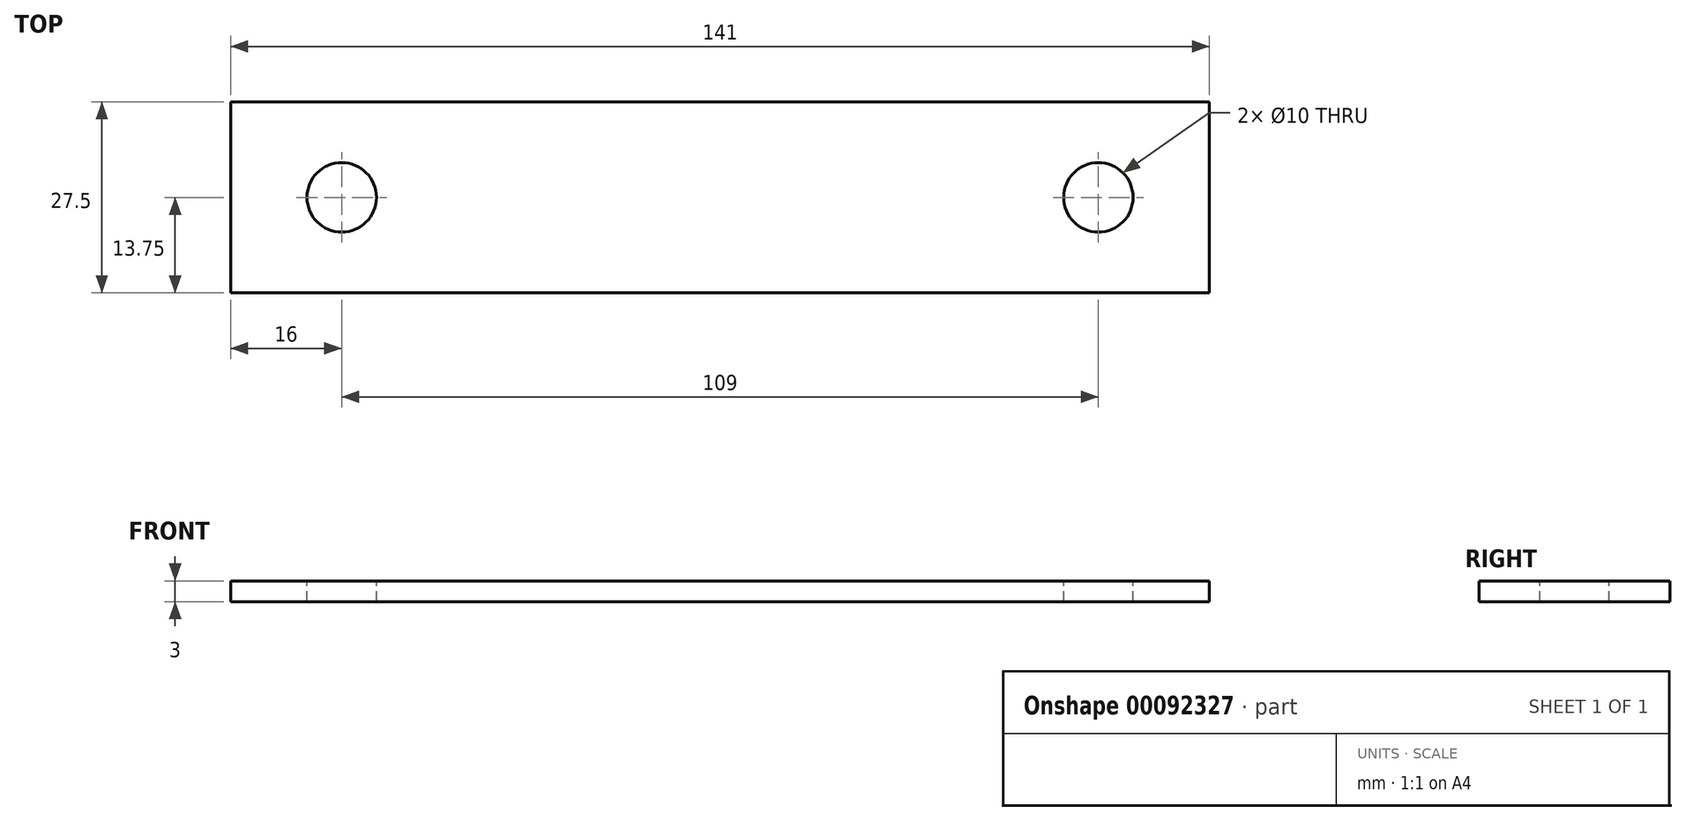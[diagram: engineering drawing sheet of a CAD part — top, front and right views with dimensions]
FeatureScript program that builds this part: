
annotation { "Feature Type Name" : "Feature", "Feature Type Description" : "" }
export const myFeature = defineFeature(function(context is Context, id is Id, definition is map)
    precondition{}
    {
        {
            var Q0;
            Q0=qCreatedBy(makeId("Top.planeOp"),FACE);
            var sketch = newSketch(context, id + "F0", { "sketchPlane" : qUnion([Q0])});
            skLineSegment(sketch, "E0.bottom", {"start": v(-70.5, 13.75) * mm, "end": v(70.5, 13.75) * mm});
            skLineSegment(sketch, "E0.top", {"start": v(-70.5, -13.75) * mm, "end": v(70.5, -13.75) * mm});
            skLineSegment(sketch, "E0.left", {"start": v(-70.5, 13.75) * mm, "end": v(-70.5, -13.75) * mm});
            skLineSegment(sketch, "E0.right", {"start": v(70.5, 13.75) * mm, "end": v(70.5, -13.75) * mm});
            skSolve(sketch);
        }
        {
            var Q0;
            Q0=makeQuery(id+"F0.imprint","IMPRINT",FACE,{"disambiguationData":[TD([[makeQuery(id+"F0.imprint","IMPRINT",EDGE,{"derivedFrom":sQuery(id+"F0.wireOp",EDGE,"E0.bottom")}),-1.0]])]});
            extrude(context, id + "F1", {"entities" : qUnion([Q0]), "endBound" : BoundingType.SYMMETRIC, "depth" : 3 * mm});
        }
        {
            var Q0;
            Q0=makeQuery(id+"F1.opExtrude","CAP_FACE",FACE,{"disambiguationData":[OSD([sQuery(id+"F0.wireOp",EDGE,"E0.bottom"),sQuery(id+"F0.wireOp",EDGE,"E0.top"),sQuery(id+"F0.wireOp",EDGE,"E0.left"),sQuery(id+"F0.wireOp",EDGE,"E0.right")])],"isStart":false});
            var sketch = newSketch(context, id + "F2", { "sketchPlane" : qUnion([Q0])});
            skCircle(sketch, "E1", {"center": v(54.5, 0) * mm, "radius": 5 * mm});
            skCircle(sketch, "E2.MirrorC", {"center": v(-54.5, 0) * mm, "radius": 5 * mm});
            skSolve(sketch);
        }
        {
            var Q0;
            Q0 = qSketchRegion(id + "F2", true);
            extrude(context, id + "F3", {"entities" : qUnion([Q0]), "operationType" : NewBodyOperationType.REMOVE, "endBound" : BoundingType.UP_TO_NEXT, "oppositeDirection" : true, "depth" : 25 * mm});
        }
    });
